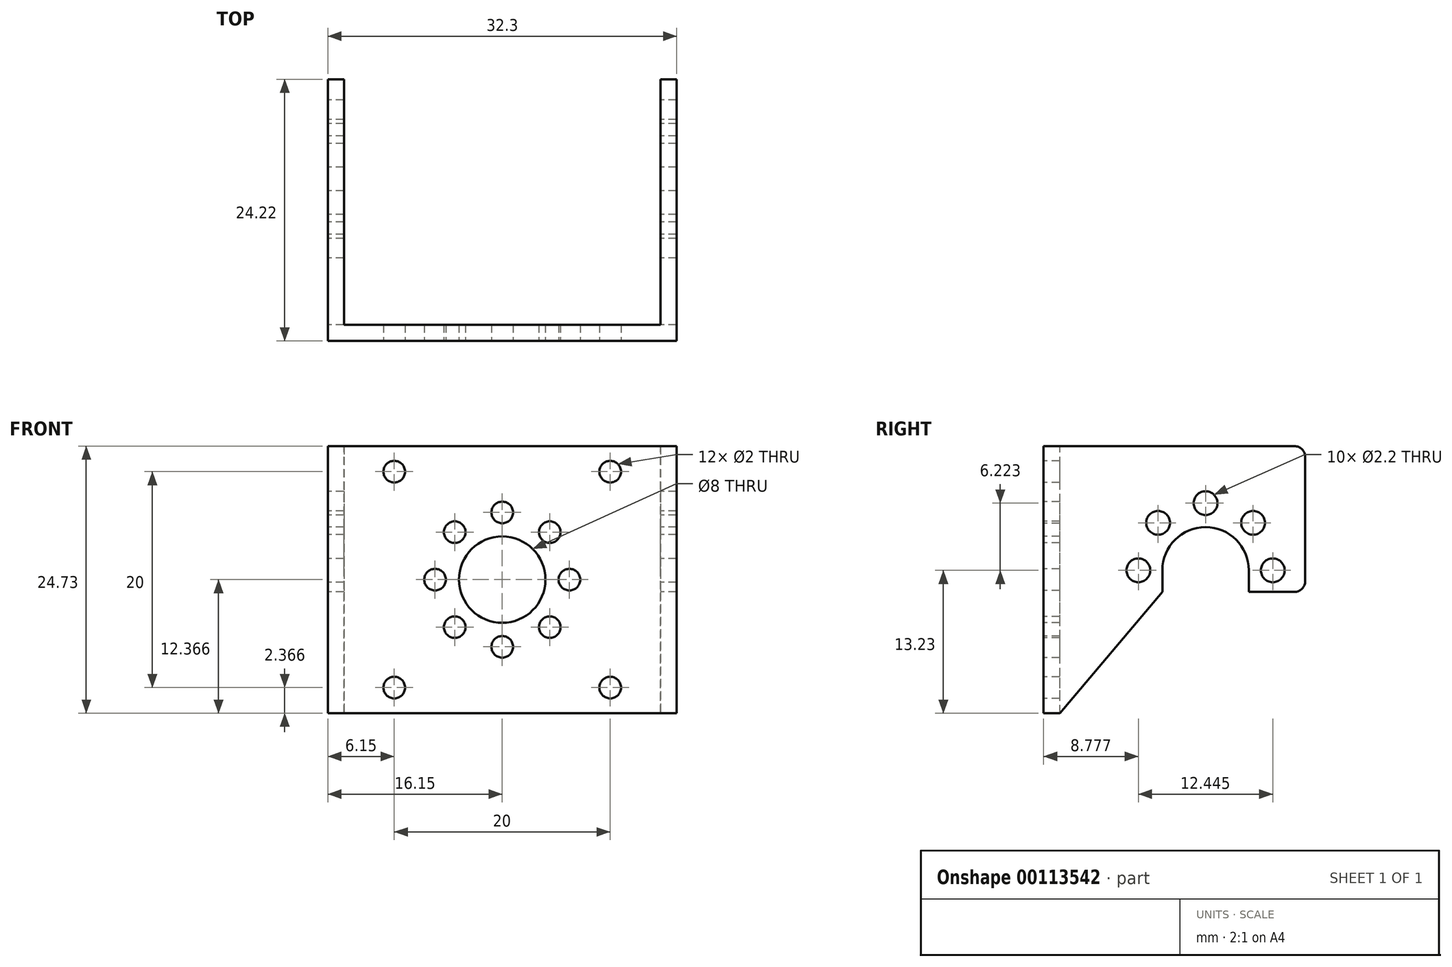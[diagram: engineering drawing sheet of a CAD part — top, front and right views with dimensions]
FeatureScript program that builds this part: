
annotation { "Feature Type Name" : "Feature", "Feature Type Description" : "" }
export const myFeature = defineFeature(function(context is Context, id is Id, definition is map)
    precondition{}
    {
        {
            var Q0;
            Q0=qCreatedBy(makeId("Front.planeOp"),FACE);
            var sketch = newSketch(context, id + "F0", { "sketchPlane" : qUnion([Q0])});
            skLineSegment(sketch, "E0.bottom", {"start": v(0, 0) * mm, "end": v(1.5, 0) * mm});
            skLineSegment(sketch, "E0.top", {"start": v(0, 41.5) * mm, "end": v(32.3, 41.5) * mm});
            skLineSegment(sketch, "E0.left", {"start": v(0, 0) * mm, "end": v(0, 41.5) * mm});
            skLineSegment(sketch, "E0.right", {"start": v(32.3, 0) * mm, "end": v(32.3, 41.5) * mm});
            skLineSegment(sketch, "E1.top", {"start": v(1.5, 40) * mm, "end": v(30.8, 40) * mm});
            skLineSegment(sketch, "E1.left", {"start": v(1.5, 0) * mm, "end": v(1.5, 40) * mm});
            skLineSegment(sketch, "E1.right", {"start": v(30.8, 0) * mm, "end": v(30.8, 40) * mm});
            skLineSegment(sketch, "E2.trimOffspring", {"start": v(30.8, 0) * mm, "end": v(32.3, 0) * mm});
            skSolve(sketch);
        }
        {
            var Q0;
            Q0=qSketchRegion(id+"F0",true);
            extrude(context, id + "F1", {"entities" : qUnion([Q0]), "depth" : 30 * mm});
        }
        {
            var Q0;
            Q0=makeQuery(id+"F1.opExtrude","SWEPT_FACE",FACE,{"disambiguationData":[OSD([sQuery(id+"F0.wireOp",EDGE,"E0.left")])]});
            var sketch = newSketch(context, id + "F2", { "sketchPlane" : qUnion([Q0])});
            skArc(sketch, "E3", {"start": v(19, 15) * mm, "mid": v(15, 19) * mm, "end": v(11, 15) * mm});
            skCircle(sketch, "E4", {"center": v(21.22, 15) * mm, "radius": 1.1 * mm});
            skCircle(sketch, "E5.1.0", {"center": v(19.4, 19.4) * mm, "radius": 1.1 * mm});
            skCircle(sketch, "E5.2.0", {"center": v(15, 21.22) * mm, "radius": 1.1 * mm});
            skCircle(sketch, "E5.3.0", {"center": v(10.6, 19.4) * mm, "radius": 1.1 * mm});
            skCircle(sketch, "E5.4.0", {"center": v(8.78, 15) * mm, "radius": 1.1 * mm});
            skLineSegment(sketch, "E6", {"start": v(11, 15) * mm, "end": v(11, 0) * mm});
            skLineSegment(sketch, "E7", {"start": v(19, 15) * mm, "end": v(19, 0) * mm});
            skLineSegment(sketch, "E8", {"start": v(11, 0) * mm, "end": v(19, 0) * mm});
            skLineSegment(sketch, "E9", {"start": v(15, 41.5) * mm, "end": v(15, 0) * mm, "construction": true});
            skPoint(sketch, "E10", {"position": v(15, 0) * mm});
            skLineSegment(sketch, "E11", {"start": v(6.78, 0) * mm, "end": v(0, 0) * mm});
            skLineSegment(sketch, "E12", {"start": v(0, 0) * mm, "end": v(0, 40) * mm});
            skLineSegment(sketch, "E13.MirrorCS", {"start": v(30, 0) * mm, "end": v(30, 40) * mm});
            skLineSegment(sketch, "E14.MirrorCS", {"start": v(23.22, 0) * mm, "end": v(30, 0) * mm});
            skPoint(sketch, "E15.MirrorCS.end.orphan", {"position": v(30, 40) * mm});
            skPoint(sketch, "E15.MirrorCS.start.orphan", {"position": v(23.22, 0) * mm});
            skSolve(sketch);
        }
        {
            var Q0;
            Q0=qSketchRegion(id+"F2",true);
            extrude(context, id + "F3", {"entities" : qUnion([Q0]), "operationType" : NewBodyOperationType.REMOVE, "endBound" : BoundingType.THROUGH_ALL, "oppositeDirection" : true, "depth" : 25 * mm});
        }
        {
            var Q0;
            Q0=makeQuery(id+"F1.opExtrude","SWEPT_FACE",FACE,{"disambiguationData":[OSD([sQuery(id+"F0.wireOp",EDGE,"E1.top")])]});
            var sketch = newSketch(context, id + "F4", { "sketchPlane" : qUnion([Q0])});
            skLineSegment(sketch, "E16.bottom", {"start": v(1.5, 30) * mm, "end": v(30.8, 30) * mm});
            skLineSegment(sketch, "E16.top", {"start": v(1.5, 28.5) * mm, "end": v(30.8, 28.5) * mm});
            skLineSegment(sketch, "E16.left", {"start": v(1.5, 30) * mm, "end": v(1.5, 28.5) * mm});
            skLineSegment(sketch, "E16.right", {"start": v(30.8, 30) * mm, "end": v(30.8, 28.5) * mm});
            skSolve(sketch);
        }
        {
            var Q0;
            Q0=qSketchRegion(id+"F4",true);
            extrude(context, id + "F5", {"entities" : qUnion([Q0]), "operationType" : NewBodyOperationType.ADD, "depth" : 40 * mm});
        }
        {
            var Q0;
            Q0=makeQuery(id+"F1.opExtrude","SWEPT_FACE",FACE,{"disambiguationData":[OSD([sQuery(id+"F0.wireOp",EDGE,"E0.left")])]});
            var sketch = newSketch(context, id + "F6", { "sketchPlane" : qUnion([Q0])});
            skLineSegment(sketch, "E17.bottom", {"start": v(0, 41.5) * mm, "end": v(30, 41.5) * mm});
            skLineSegment(sketch, "E17.top", {"start": v(5.78, 26.5) * mm, "end": v(30, 26.5) * mm});
            skLineSegment(sketch, "E17.left", {"start": v(0, 41.5) * mm, "end": v(0, 26.5) * mm});
            skLineSegment(sketch, "E17.right", {"start": v(30, 41.5) * mm, "end": v(30, 26.5) * mm});
            skLineSegment(sketch, "E18.top", {"start": v(0, 0) * mm, "end": v(5.78, 0) * mm});
            skLineSegment(sketch, "E18.left", {"start": v(0, 26.5) * mm, "end": v(0, 0) * mm});
            skLineSegment(sketch, "E18.right", {"start": v(5.78, 26.5) * mm, "end": v(5.78, 0) * mm});
            skPoint(sketch, "E19", {"position": v(8.78, 15) * mm});
            skLineSegment(sketch, "E20.bottom", {"start": v(5.78, 0) * mm, "end": v(11, 0) * mm});
            skLineSegment(sketch, "E20.top", {"start": v(5.78, 13) * mm, "end": v(11, 13) * mm});
            skLineSegment(sketch, "E20.left", {"start": v(5.78, 0) * mm, "end": v(5.78, 13) * mm});
            skLineSegment(sketch, "E20.right", {"start": v(11, 0) * mm, "end": v(11, 13) * mm});
            skLineSegment(sketch, "E21", {"start": v(19, 13) * mm, "end": v(30, 0) * mm});
            skLineSegment(sketch, "E22", {"start": v(30, 0) * mm, "end": v(19, 0) * mm});
            skLineSegment(sketch, "E23", {"start": v(19, 0) * mm, "end": v(19, 13) * mm});
            skLineSegment(sketch, "E24", {"start": v(30, 1.77) * mm, "end": v(28.5, 1.77) * mm});
            skSolve(sketch);
        }
        {
            var Q0;
            Q0=qSketchRegion(id+"F6",true);
            var Q1;
            {var subQ3=sQuery(id+"F6.wireOp",EDGE,"E24");Q1=makeQuery(id+"F6.imprint","IMPRINT",FACE,{"disambiguationData":[TD([[makeQuery(id+"F6.imprint","IMPRINT",EDGE,{"derivedFrom":subQ3}),1.0]])]});}
            extrude(context, id + "F7", {"entities" : qUnion([Q0, Q1]), "operationType" : NewBodyOperationType.REMOVE, "endBound" : BoundingType.THROUGH_ALL, "oppositeDirection" : true, "depth" : 25 * mm});
        }
        {
            var Q0;
            Q0=makeQuery(id+"F5.boolean.opBoolean","MERGE",FACE,{"derivedFrom":[makeQuery(id+"F1.opExtrude","CAP_FACE",FACE,{"disambiguationData":[OSD([sQuery(id+"F0.wireOp",EDGE,"E0.bottom"),sQuery(id+"F0.wireOp",EDGE,"E0.top"),sQuery(id+"F0.wireOp",EDGE,"E0.left"),sQuery(id+"F0.wireOp",EDGE,"E0.right"),sQuery(id+"F0.wireOp",EDGE,"E1.top"),sQuery(id+"F0.wireOp",EDGE,"E1.left"),sQuery(id+"F0.wireOp",EDGE,"E1.right"),sQuery(id+"F0.wireOp",EDGE,"E2.trimOffspring")])],"isStart":false}),makeQuery(id+"F5.opExtrude","SWEPT_FACE",FACE,{"disambiguationData":[OSD([sQuery(id+"F4.wireOp",EDGE,"E16.bottom")])]})]});
            var sketch = newSketch(context, id + "F8", { "sketchPlane" : qUnion([Q0])});
            skLineSegment(sketch, "E25", {"start": v(0, 14.14) * mm, "end": v(32.3, 14.14) * mm, "construction": true});
            skCircle(sketch, "E26", {"center": v(6.15, 24.14) * mm, "radius": 1 * mm});
            skCircle(sketch, "E27.MirrorC", {"center": v(6.15, 4.14) * mm, "radius": 1 * mm});
            skLineSegment(sketch, "E28.0", {"start": v(32.3, 26.5) * mm, "end": v(0, 26.5) * mm, "construction": true});
            skLineSegment(sketch, "E29.0", {"start": v(32.3, 1.77) * mm, "end": v(0, 1.77) * mm, "construction": true});
            skLineSegment(sketch, "E30", {"start": v(16.15, 26.5) * mm, "end": v(16.15, 1.77) * mm, "construction": true});
            skCircle(sketch, "E31.MirrorC", {"center": v(26.15, 24.14) * mm, "radius": 1 * mm});
            skCircle(sketch, "E32.MirrorC", {"center": v(26.15, 4.14) * mm, "radius": 1 * mm});
            skCircle(sketch, "E33", {"center": v(16.15, 14.14) * mm, "radius": 4 * mm});
            skLineSegment(sketch, "E34.bottom", {"start": v(20.55, 9.74) * mm, "end": v(11.75, 9.74) * mm, "construction": true});
            skLineSegment(sketch, "E34.top", {"start": v(20.55, 18.54) * mm, "end": v(11.75, 18.54) * mm, "construction": true});
            skLineSegment(sketch, "E34.left", {"start": v(20.55, 9.74) * mm, "end": v(20.55, 18.54) * mm, "construction": true});
            skLineSegment(sketch, "E34.right", {"start": v(11.75, 9.74) * mm, "end": v(11.75, 18.54) * mm, "construction": true});
            skCircle(sketch, "E35", {"center": v(20.55, 18.54) * mm, "radius": 1 * mm});
            skCircle(sketch, "E36.1.0", {"center": v(16.15, 20.36) * mm, "radius": 1 * mm});
            skCircle(sketch, "E36.2.0", {"center": v(11.75, 18.54) * mm, "radius": 1 * mm});
            skCircle(sketch, "E36.3.0", {"center": v(9.93, 14.14) * mm, "radius": 1 * mm});
            skCircle(sketch, "E36.4.0", {"center": v(11.75, 9.74) * mm, "radius": 1 * mm});
            skCircle(sketch, "E36.5.0", {"center": v(16.15, 7.91) * mm, "radius": 1 * mm});
            skCircle(sketch, "E36.6.0", {"center": v(20.55, 9.74) * mm, "radius": 1 * mm});
            skCircle(sketch, "E36.7.0", {"center": v(22.37, 14.14) * mm, "radius": 1 * mm});
            skSolve(sketch);
        }
        {
            var Q0;
            Q0=qSketchRegion(id+"F8",true);
            extrude(context, id + "F9", {"entities" : qUnion([Q0]), "operationType" : NewBodyOperationType.REMOVE, "endBound" : BoundingType.UP_TO_NEXT, "oppositeDirection" : true, "depth" : 25 * mm});
        }
        {
            var Q0;
            Q0=makeQuery(id+"F7.boolean.opBoolean","COPY",EDGE,{"disambiguationData":[OD(0.0)],"derivedFrom":makeQuery(id+"F7.opExtrude","SWEPT_EDGE",EDGE,{"disambiguationData":[OSD([sQuery(id+"F6.wireOp",EDGE,"E18.right"),sQuery(id+"F6.wireOp",EDGE,"E20.top"),sQuery(id+"F6.wireOp",EDGE,"E20.left")])]})});
            var Q1;
            Q1=makeQuery(id+"F7.boolean.opBoolean","COPY",EDGE,{"disambiguationData":[OD(0.0)],"derivedFrom":makeQuery(id+"F7.opExtrude","SWEPT_EDGE",EDGE,{"disambiguationData":[OSD([sQuery(id+"F2.wireOp",EDGE,"E7"),sQuery(id+"F6.wireOp",EDGE,"E21"),sQuery(id+"F6.wireOp",EDGE,"E23")])]})});
            var Q2;
            Q2=makeQuery(id+"F7.boolean.opBoolean","COPY",EDGE,{"disambiguationData":[OD(1.0)],"derivedFrom":makeQuery(id+"F7.opExtrude","SWEPT_EDGE",EDGE,{"disambiguationData":[OSD([sQuery(id+"F2.wireOp",EDGE,"E7"),sQuery(id+"F6.wireOp",EDGE,"E21"),sQuery(id+"F6.wireOp",EDGE,"E23")])]})});
            var Q3;
            Q3=makeQuery(id+"F7.boolean.opBoolean","COPY",EDGE,{"disambiguationData":[OD(1.0)],"derivedFrom":makeQuery(id+"F7.opExtrude","SWEPT_EDGE",EDGE,{"disambiguationData":[OSD([sQuery(id+"F6.wireOp",EDGE,"E18.right"),sQuery(id+"F6.wireOp",EDGE,"E20.top"),sQuery(id+"F6.wireOp",EDGE,"E20.left")])]})});
            var Q4;
            Q4=makeQuery(id+"F7.boolean.opBoolean","COPY",EDGE,{"disambiguationData":[OD(0.0)],"derivedFrom":makeQuery(id+"F7.opExtrude","SWEPT_EDGE",EDGE,{"disambiguationData":[OSD([sQuery(id+"F2.wireOp",EDGE,"E6"),sQuery(id+"F6.wireOp",EDGE,"E20.top"),sQuery(id+"F6.wireOp",EDGE,"E20.right")])]})});
            var Q5;
            Q5=makeQuery(id+"F7.boolean.opBoolean","COPY",EDGE,{"disambiguationData":[OD(1.0)],"derivedFrom":makeQuery(id+"F7.opExtrude","SWEPT_EDGE",EDGE,{"disambiguationData":[OSD([sQuery(id+"F2.wireOp",EDGE,"E6"),sQuery(id+"F6.wireOp",EDGE,"E20.top"),sQuery(id+"F6.wireOp",EDGE,"E20.right")])]})});
            var Q6;
            Q6=makeQuery(id+"F7.boolean.opBoolean","COPY",EDGE,{"disambiguationData":[OD(0.0)],"derivedFrom":makeQuery(id+"F7.opExtrude","SWEPT_EDGE",EDGE,{"disambiguationData":[OSD([sQuery(id+"F6.wireOp",EDGE,"E17.top"),sQuery(id+"F6.wireOp",EDGE,"E18.right")])]})});
            var Q7;
            Q7=makeQuery(id+"F7.boolean.opBoolean","COPY",EDGE,{"disambiguationData":[OD(1.0)],"derivedFrom":makeQuery(id+"F7.opExtrude","SWEPT_EDGE",EDGE,{"disambiguationData":[OSD([sQuery(id+"F6.wireOp",EDGE,"E17.top"),sQuery(id+"F6.wireOp",EDGE,"E18.right")])]})});
            fillet(context, id + "F10", {"entities" : qUnion([Q0, Q1, Q2, Q3, Q4, Q5, Q6, Q7]), "radius" : 1 * mm, "tangentPropagation" : true, "allowEdgeOverflow" : false});
        }
    });
